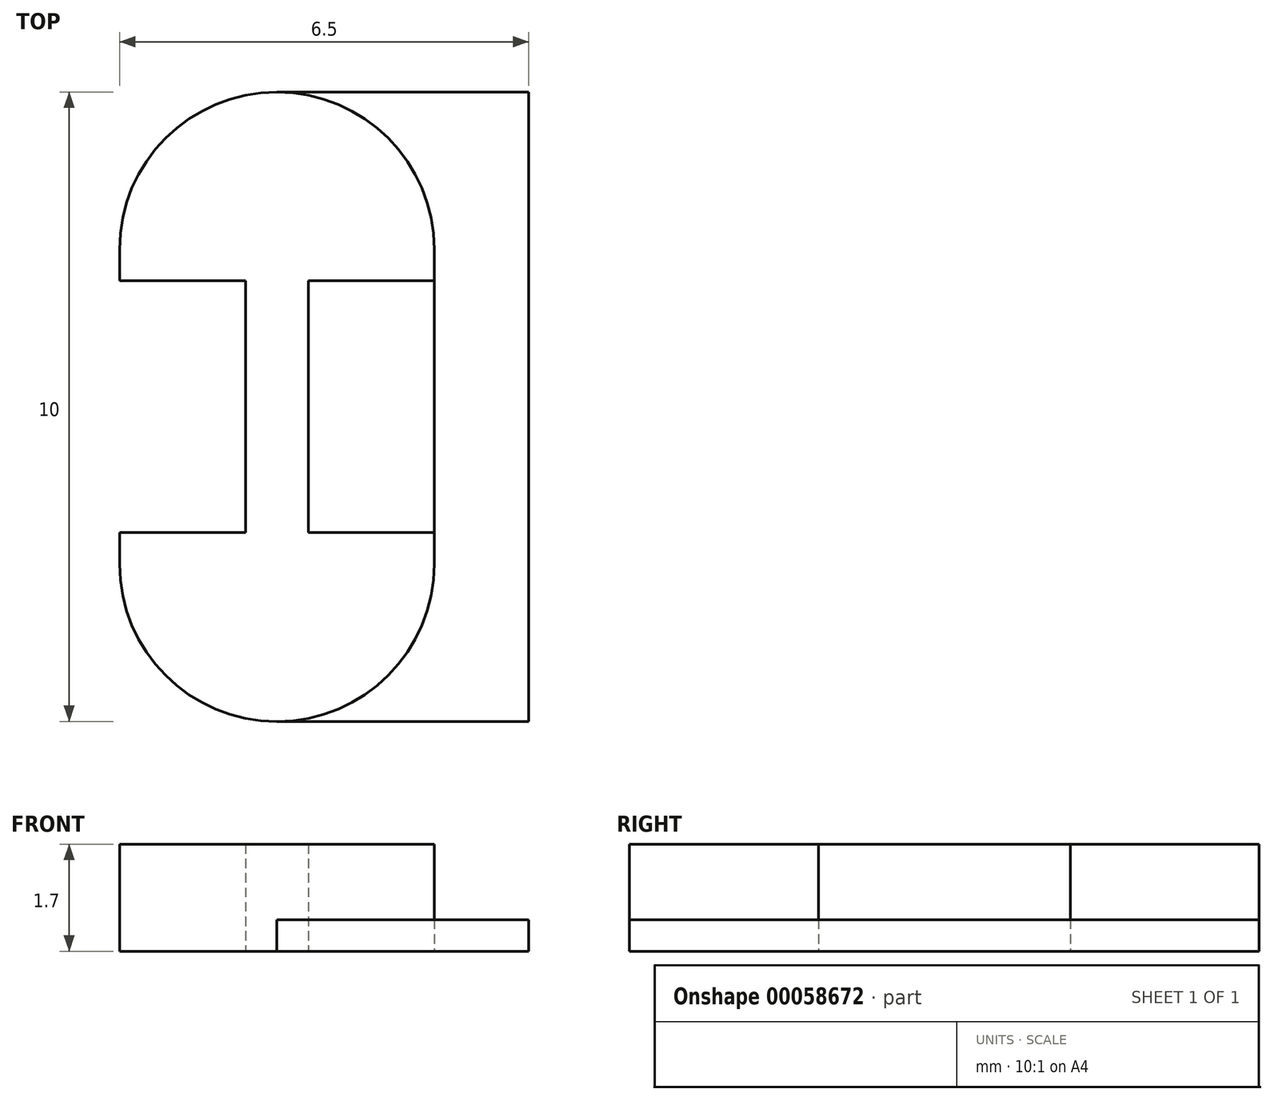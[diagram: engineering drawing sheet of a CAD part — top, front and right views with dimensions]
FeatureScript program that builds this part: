
annotation { "Feature Type Name" : "Feature", "Feature Type Description" : "" }
export const myFeature = defineFeature(function(context is Context, id is Id, definition is map)
    precondition{}
    {
        {
            var Q0;
            Q0=qCreatedBy(makeId("Top.planeOp"),FACE);
            var sketch = newSketch(context, id + "F0", { "sketchPlane" : qUnion([Q0])});
            skLineSegment(sketch, "E0.rect.bottom", {"start": v(0, 5) * mm, "end": v(0, 5) * mm});
            skLineSegment(sketch, "E0.rect.top", {"start": v(0, -5) * mm, "end": v(0, -5) * mm});
            skLineSegment(sketch, "E0.rect.left", {"start": v(2.5, 2.5) * mm, "end": v(2.5, -2.5) * mm});
            skLineSegment(sketch, "E0.rect.right", {"start": v(-2.5, 2.5) * mm, "end": v(-2.5, -2.5) * mm});
            skPoint(sketch, "E0.rect.middle", {"position": v(0, 0) * mm});
            skLineSegment(sketch, "E1.rect.bottom", {"start": v(-2.5, 2) * mm, "end": v(-0.5, 2) * mm});
            skLineSegment(sketch, "E1.rect.top", {"start": v(-2.5, -2) * mm, "end": v(-0.5, -2) * mm});
            skLineSegment(sketch, "E1.rect.left", {"start": v(-2.5, 2) * mm, "end": v(-2.5, -2) * mm});
            skLineSegment(sketch, "E1.rect.right", {"start": v(-0.5, 2) * mm, "end": v(-0.5, -2) * mm});
            skPoint(sketch, "E1.rect.middle", {"position": v(-1.5, 0) * mm});
            skLineSegment(sketch, "E2.MirrorCS", {"start": v(2.5, 2) * mm, "end": v(0.5, 2) * mm});
            skLineSegment(sketch, "E3.MirrorCS", {"start": v(0.5, 2) * mm, "end": v(0.5, -2) * mm});
            skLineSegment(sketch, "E4.MirrorCS", {"start": v(2.5, -2) * mm, "end": v(0.5, -2) * mm});
            skPoint(sketch, "E5.visualSharp", {"position": v(-2.5, 5) * mm});
            skArc(sketch, "E5.filletArc", {"start": v(0, 5) * mm, "mid": v(-1.77, 4.27) * mm, "end": v(-2.5, 2.5) * mm});
            skPoint(sketch, "E6.visualSharp", {"position": v(2.5, 5) * mm});
            skArc(sketch, "E6.filletArc", {"start": v(2.5, 2.5) * mm, "mid": v(1.77, 4.27) * mm, "end": v(0, 5) * mm});
            skPoint(sketch, "E7.visualSharp", {"position": v(-2.5, -5) * mm});
            skArc(sketch, "E7.filletArc", {"start": v(-2.5, -2.5) * mm, "mid": v(-1.77, -4.27) * mm, "end": v(0, -5) * mm});
            skPoint(sketch, "E8.visualSharp", {"position": v(2.5, -5) * mm});
            skArc(sketch, "E8.filletArc", {"start": v(0, -5) * mm, "mid": v(1.77, -4.27) * mm, "end": v(2.5, -2.5) * mm});
            skLineSegment(sketch, "E9.rect.bottom", {"start": v(-4, 5) * mm, "end": v(4, 5) * mm});
            skLineSegment(sketch, "E9.rect.top", {"start": v(-4, -5) * mm, "end": v(4, -5) * mm});
            skLineSegment(sketch, "E9.rect.left", {"start": v(-4, 5) * mm, "end": v(-4, -5) * mm});
            skLineSegment(sketch, "E9.rect.right", {"start": v(4, 5) * mm, "end": v(4, -5) * mm});
            skSolve(sketch);
        }
        {
            var Q0;
            {var subQ3=sQuery(id+"F0.wireOp",EDGE,"E1.rect.left");Q0=makeQuery(id+"F0.imprint","IMPRINT",FACE,{"disambiguationData":[TD([[makeQuery(id+"F0.imprint","IMPRINT",EDGE,{"derivedFrom":subQ3}),-1.0]])]});}
            var Q1;
            {var subQ0=sQuery(id+"F0.wireOp",EDGE,"E6.filletArc");Q1=makeQuery(id+"F0.imprint","IMPRINT",FACE,{"disambiguationData":[TD([[makeQuery(id+"F0.imprint","IMPRINT",EDGE,{"derivedFrom":subQ0}),-1.0]])]});}
            extrude(context, id + "F1", {"entities" : qUnion([Q0, Q1]), "depth" : 0.5 * mm});
        }
        {
            var Q0;
            {var subQ3=sQuery(id+"F0.wireOp",EDGE,"E1.rect.bottom");Q0=makeQuery(id+"F0.imprint","IMPRINT",FACE,{"disambiguationData":[TD([[makeQuery(id+"F0.imprint","IMPRINT",EDGE,{"derivedFrom":subQ3}),1.0]])]});}
            extrude(context, id + "F2", {"entities" : qUnion([Q0]), "depth" : 1.7 * mm});
        }
    });
